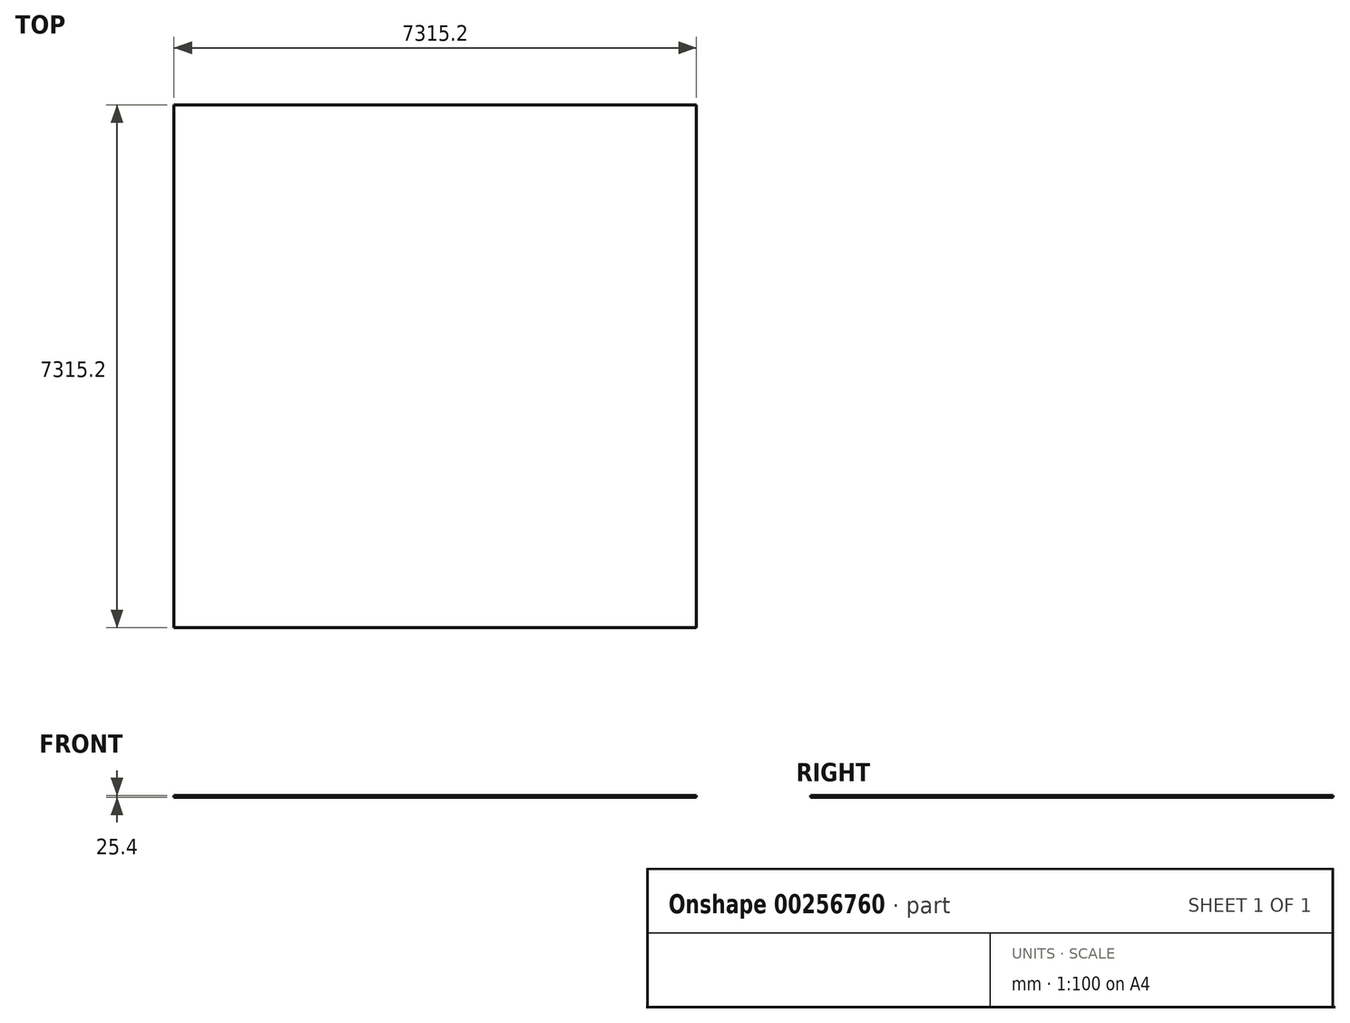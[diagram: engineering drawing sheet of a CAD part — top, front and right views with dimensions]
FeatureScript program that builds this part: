
annotation { "Feature Type Name" : "Feature", "Feature Type Description" : "" }
export const myFeature = defineFeature(function(context is Context, id is Id, definition is map)
    precondition{}
    {
        {
            var Q0;
            Q0=qCreatedBy(makeId("Top.planeOp"),FACE);
            var sketch = newSketch(context, id + "F0", { "sketchPlane" : qUnion([Q0])});
            skLineSegment(sketch, "E0.bottom", {"start": v(3657.6, 3657.6) * mm, "end": v(-3657.6, 3657.6) * mm});
            skLineSegment(sketch, "E0.top", {"start": v(3657.6, -3657.6) * mm, "end": v(-3657.6, -3657.6) * mm});
            skLineSegment(sketch, "E0.left", {"start": v(3657.6, 3657.6) * mm, "end": v(3657.6, -3657.6) * mm});
            skLineSegment(sketch, "E0.right", {"start": v(-3657.6, 3657.6) * mm, "end": v(-3657.6, -3657.6) * mm});
            skPoint(sketch, "E0.middle", {"position": v(0, 0) * mm});
            skSolve(sketch);
        }
        {
            var Q0;
            Q0=makeQuery(id+"F0.imprint","IMPRINT",FACE,{"disambiguationData":[TD([[makeQuery(id+"F0.imprint","IMPRINT",EDGE,{"derivedFrom":sQuery(id+"F0.wireOp",EDGE,"E0.bottom")}),1.0]])]});
            extrude(context, id + "F1", {"entities" : qUnion([Q0]), "oppositeDirection" : true, "depth" : 25.4 * mm});
        }
    });
